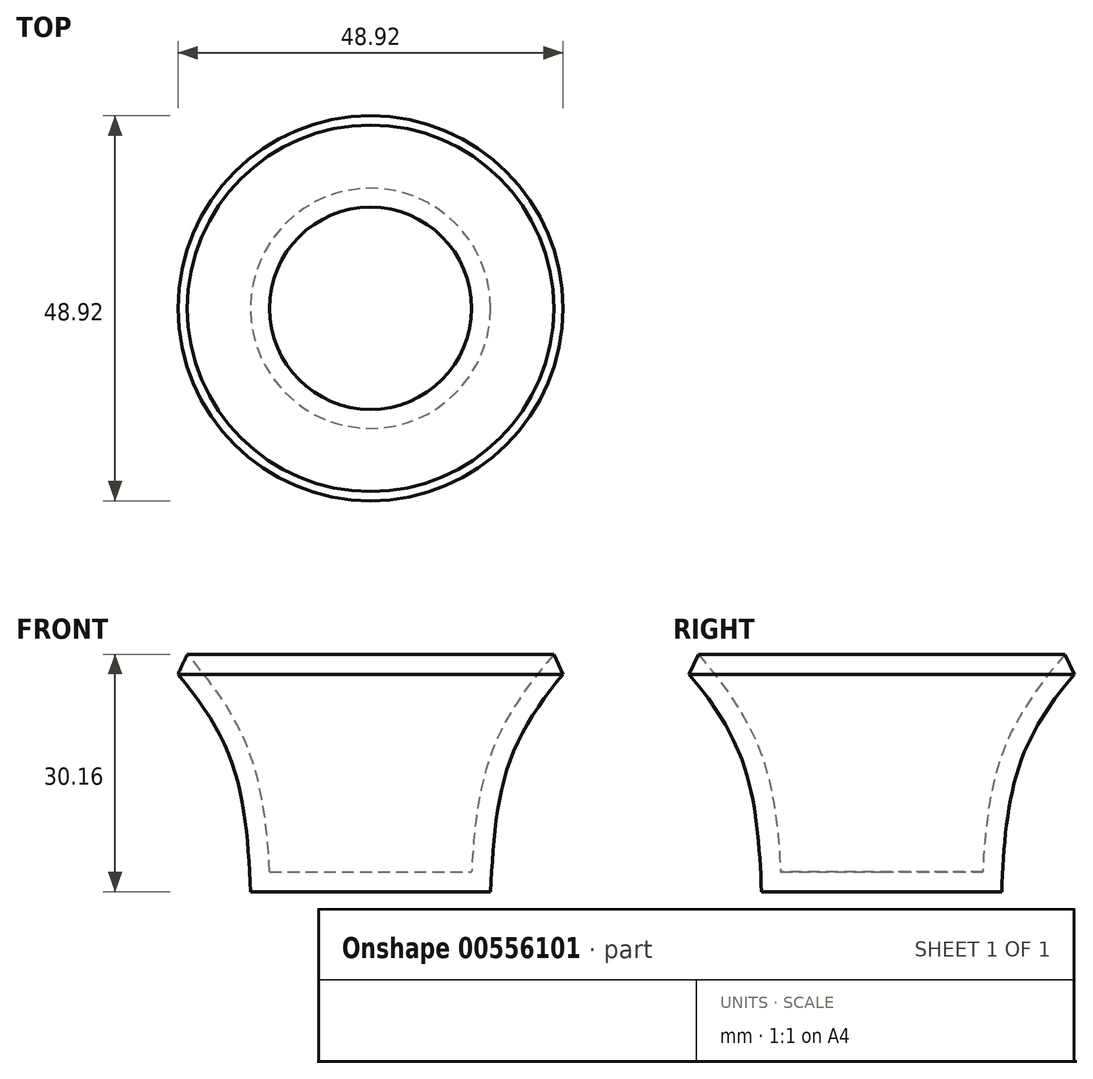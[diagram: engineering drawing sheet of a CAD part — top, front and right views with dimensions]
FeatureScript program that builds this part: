
annotation { "Feature Type Name" : "Feature", "Feature Type Description" : "" }
export const myFeature = defineFeature(function(context is Context, id is Id, definition is map)
    precondition{}
    {
        {
            var Q0;
            Q0=qCreatedBy(makeId("Front.planeOp"),FACE);
            var sketch = newSketch(context, id + "F0", { "sketchPlane" : qUnion([Q0])});
            skLineSegment(sketch, "E0", {"start": v(0, 0) * mm, "end": v(0, 35.98) * mm});
            skLineSegment(sketch, "E1", {"start": v(0, 35.98) * mm, "end": v(32.23, 35.98) * mm});
            skLineSegment(sketch, "E2", {"start": v(0, 0) * mm, "end": v(15.25, 0) * mm});
            skFitSpline(sketch, "E3", {"points": [v(15.25, 0) * mm, v(18.42, 18.42) * mm, v(32.23, 35.98) * mm], "startDerivative": vector(1.9, 39.74) * mm, "endDerivative": vector(31.63, 32.32) * mm});
            skSolve(sketch);
        }
        {
            var Q0;
            Q0=makeQuery(id+"F0.imprint","IMPRINT",FACE,{"disambiguationData":[TD([[makeQuery(id+"F0.imprint","IMPRINT",EDGE,{"derivedFrom":sQuery(id+"F0.wireOp",EDGE,"E0")}),-1.0]])]});
            var Q1;
            Q1=sQuery(id+"F0.wireOp",EDGE,"E0");
            revolve(context, id + "F1", {"entities" : qUnion([Q0]), "axis" : qUnion([Q1]), "revolveType" : RevolveType.FULL});
        }
        {
            var Q0;
            Q0=makeQuery(id+"F1.opRevolve","SWEPT_FACE",FACE,{"disambiguationData":[OSD([sQuery(id+"F0.wireOp",EDGE,"E1")])]});
            shell(context, id + "F2", {"entities" : qUnion([Q0]), "thickness" : 2.54 * mm});
        }
        {
            var Q0;
            Q0=makeQuery(id+"F1.opRevolve","SWEPT_EDGE",EDGE,{"disambiguationData":[OSD([sQuery(id+"F0.wireOp",EDGE,"E1"),sQuery(id+"F0.wireOp",EDGE,"E3")])]});
            chamfer(context, id + "F3", {"entities" : qUnion([Q0]), "width" : 5.08 * mm, "tangentPropagation" : true});
        }
    });
